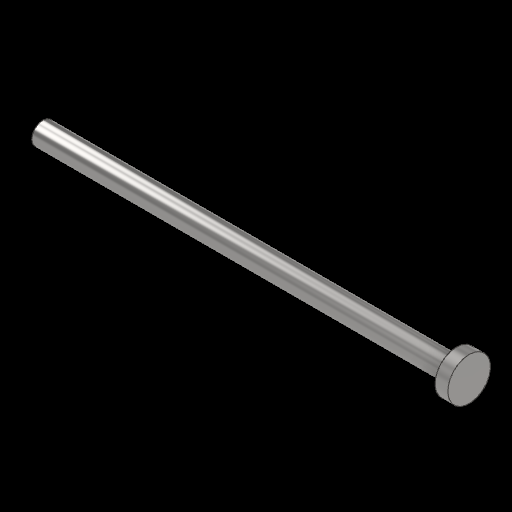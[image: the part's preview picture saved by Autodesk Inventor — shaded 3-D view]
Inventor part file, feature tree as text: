
AUTODESK INVENTOR PART (.ipt)
format: ipt  version: 2024 (Build 280153000, 153)  size: 113,664 bytes
history: native  units: mm
features: revolve x1, sketch x1
ambient origin geometry x8: Origin, YZ Plane, XZ Plane, XY Plane, X Axis, Y Axis, Z Axis, Center Point
bodies: Volumenkörper1 (feature_tree)
feature tree (2):
  revolve  "Umdrehung1"
  sketch  "Skizze1"  dims[d0=5.2mm d1=100.0mm d2=10.0mm d3=3.0mm d4=0.3mm d5=90.0deg]
